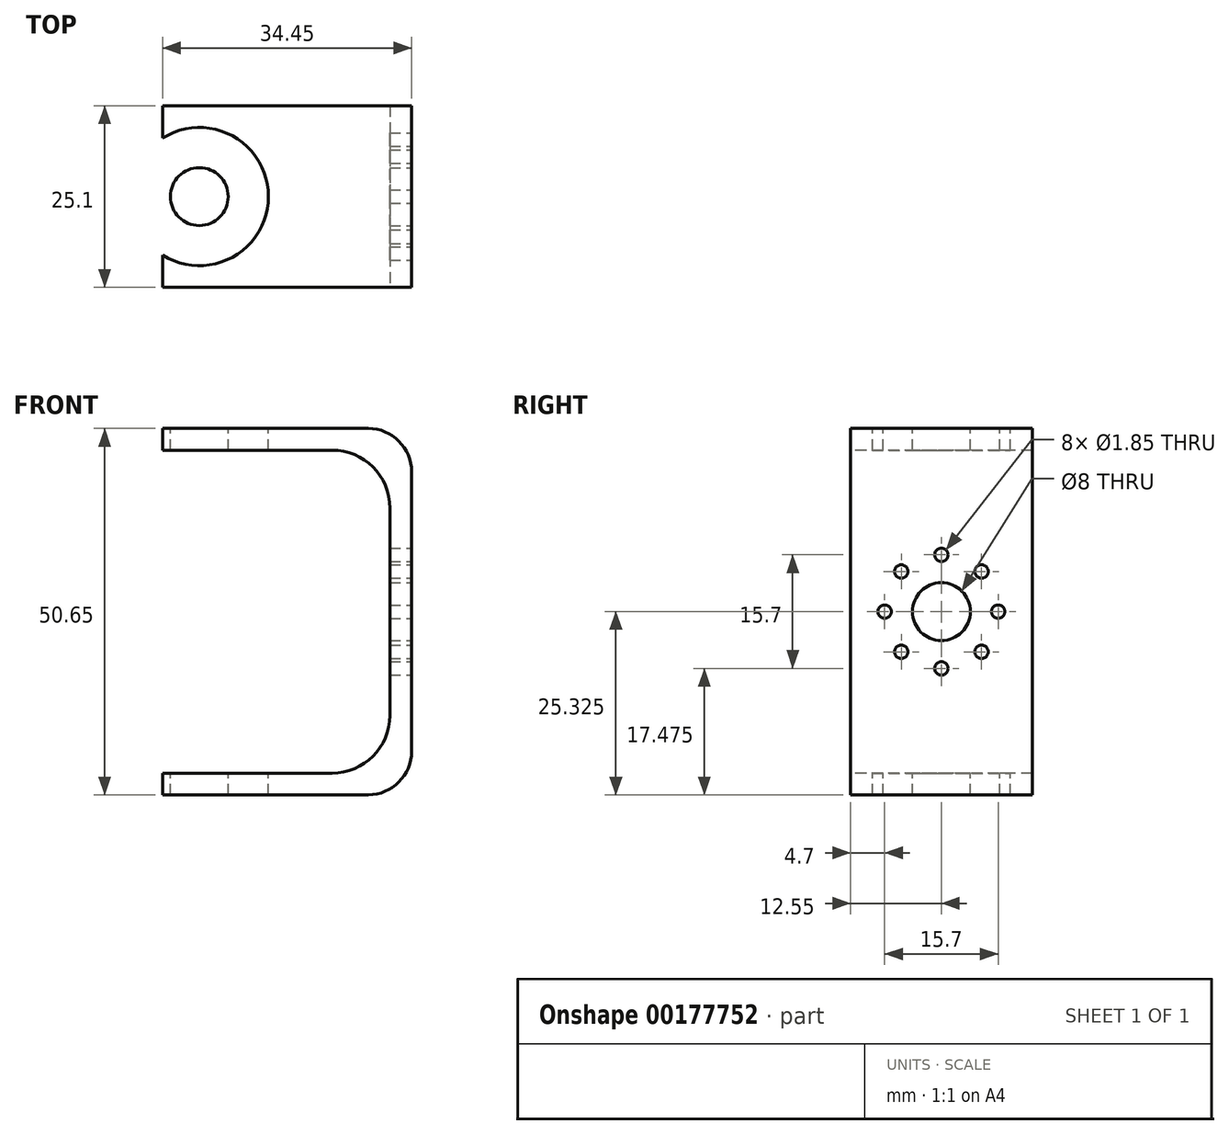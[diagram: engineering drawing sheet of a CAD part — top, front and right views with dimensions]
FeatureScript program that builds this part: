
annotation { "Feature Type Name" : "Feature", "Feature Type Description" : "" }
export const myFeature = defineFeature(function(context is Context, id is Id, definition is map)
    precondition{}
    {
        {
            var Q0;
            Q0=qCreatedBy(makeId("Top.planeOp"),FACE);
            var sketch = newSketch(context, id + "F0", { "sketchPlane" : qUnion([Q0])});
            skLineSegment(sketch, "E0.bottom", {"start": v(-15.32, 25.1) * mm, "end": v(19.13, 25.1) * mm});
            skLineSegment(sketch, "E0.top", {"start": v(-15.32, 0) * mm, "end": v(19.13, 0) * mm});
            skLineSegment(sketch, "E0.left", {"start": v(-15.32, 25.1) * mm, "end": v(-15.32, 0) * mm});
            skLineSegment(sketch, "E0.right", {"start": v(19.13, 25.1) * mm, "end": v(19.13, 0) * mm});
            skSolve(sketch);
        }
        {
            var Q0;
            Q0=qSketchRegion(id+"F0",true);
            extrude(context, id + "F1", {"entities" : qUnion([Q0]), "depth" : 50.65 * mm});
        }
        {
            var Q0;
            Q0=makeQuery(id+"F1.opExtrude","SWEPT_FACE",FACE,{"disambiguationData":[OSD([sQuery(id+"F0.wireOp",EDGE,"E0.left")])]});
            shell(context, id + "F2", {"entities" : qUnion([Q0]), "thickness" : 3 * mm});
        }
        {
            var Q0;
            Q0=makeQuery(id+"F1.opExtrude","SWEPT_FACE",FACE,{"disambiguationData":[OSD([sQuery(id+"F0.wireOp",EDGE,"E0.right")])]});
            var sketch = newSketch(context, id + "F3", { "sketchPlane" : qUnion([Q0])});
            skLineSegment(sketch, "E1", {"start": v(12.55, 0) * mm, "end": v(12.55, 50.65) * mm, "construction": true});
            skCircle(sketch, "E2", {"center": v(12.55, 25.32) * mm, "radius": 4 * mm});
            skCircle(sketch, "E3", {"center": v(12.55, 17.48) * mm, "radius": 0.93 * mm});
            skCircle(sketch, "E4.1.0", {"center": v(18.1, 19.77) * mm, "radius": 0.92 * mm});
            skCircle(sketch, "E4.2.0", {"center": v(20.4, 25.32) * mm, "radius": 0.93 * mm});
            skCircle(sketch, "E4.3.0", {"center": v(18.1, 30.88) * mm, "radius": 0.93 * mm});
            skCircle(sketch, "E5.1.4.0", {"center": v(12.55, 33.18) * mm, "radius": 0.93 * mm});
            skCircle(sketch, "E5.1.5.0", {"center": v(7, 30.88) * mm, "radius": 0.93 * mm});
            skCircle(sketch, "E5.1.6.0", {"center": v(4.7, 25.32) * mm, "radius": 0.92 * mm});
            skCircle(sketch, "E5.1.7.0", {"center": v(7, 19.77) * mm, "radius": 0.93 * mm});
            skSolve(sketch);
        }
        {
            var Q0;
            Q0=qSketchRegion(id+"F3",true);
            extrude(context, id + "F4", {"entities" : qUnion([Q0]), "operationType" : NewBodyOperationType.REMOVE, "oppositeDirection" : true, "depth" : 25 * mm});
        }
        {
            var Q0;
            Q0=makeQuery(id+"F1.opExtrude","SWEPT_FACE",FACE,{"disambiguationData":[OSD([sQuery(id+"F0.wireOp",EDGE,"E0.bottom")])]});
            var sketch = newSketch(context, id + "F5", { "sketchPlane" : qUnion([Q0])});
            skLineSegment(sketch, "E6", {"start": v(15.32, 3) * mm, "end": v(-16.13, 3) * mm});
            skLineSegment(sketch, "E7", {"start": v(-16.13, 3) * mm, "end": v(-16.13, 47.65) * mm});
            skLineSegment(sketch, "E8", {"start": v(-16.13, 47.65) * mm, "end": v(15.32, 47.65) * mm});
            skSolve(sketch);
        }
        {
            var Q0;
            {var subQ0=sQuery(id+"F5.wireOp",EDGE,"E6");Q0=makeQuery(id+"F5.imprint","IMPRINT",FACE,{"disambiguationData":[TD([[makeQuery(id+"F5.imprint","IMPRINT",EDGE,{"derivedFrom":subQ0}),-1.0]])]});}
            extrude(context, id + "F6", {"entities" : qUnion([Q0]), "operationType" : NewBodyOperationType.REMOVE, "endBound" : BoundingType.THROUGH_ALL, "oppositeDirection" : true, "depth" : 25 * mm});
        }
        {
            var Q0;
            {var subQ0=sQuery(id+"F0.wireOp",EDGE,"E0.right");Q0=makeQuery(id+"F6.boolean.opBoolean","MERGE",EDGE,{"derivedFrom":[makeQuery(id+"F2.opShell","OFFSET_EDGE",EDGE,{"disambiguationData":[OSD([subQ0]),TDD([makeQuery(id+"F1.opExtrude","CAP_EDGE",EDGE,{"disambiguationData":[OSD([subQ0])],"isStart":false})])]}),makeQuery(id+"F6.opExtrude","SWEPT_EDGE",EDGE,{"disambiguationData":[OSD([sQuery(id+"F5.wireOp",EDGE,"E7"),sQuery(id+"F5.wireOp",EDGE,"E8")])]})]});}
            var Q1;
            {var subQ0=sQuery(id+"F0.wireOp",EDGE,"E0.right");Q1=makeQuery(id+"F6.boolean.opBoolean","MERGE",EDGE,{"derivedFrom":[makeQuery(id+"F2.opShell","OFFSET_EDGE",EDGE,{"disambiguationData":[OSD([subQ0]),TDD([makeQuery(id+"F1.opExtrude","CAP_EDGE",EDGE,{"disambiguationData":[OSD([subQ0])],"isStart":true})])]}),makeQuery(id+"F6.opExtrude","SWEPT_EDGE",EDGE,{"disambiguationData":[OSD([sQuery(id+"F5.wireOp",EDGE,"E6"),sQuery(id+"F5.wireOp",EDGE,"E7")])]})]});}
            fillet(context, id + "F7", {"entities" : qUnion([Q0, Q1]), "radius" : 8 * mm, "tangentPropagation" : true, "allowEdgeOverflow" : false});
        }
        {
            var Q0;
            Q0=makeQuery(id+"F1.opExtrude","CAP_EDGE",EDGE,{"disambiguationData":[OSD([sQuery(id+"F0.wireOp",EDGE,"E0.right")])],"isStart":false});
            var Q1;
            Q1=makeQuery(id+"F1.opExtrude","CAP_EDGE",EDGE,{"disambiguationData":[OSD([sQuery(id+"F0.wireOp",EDGE,"E0.right")])],"isStart":true});
            fillet(context, id + "F8", {"entities" : qUnion([Q0, Q1]), "radius" : 6 * mm, "tangentPropagation" : true, "allowEdgeOverflow" : false});
        }
        {
            var Q0;
            Q0=makeQuery(id+"F1.opExtrude","CAP_FACE",FACE,{"disambiguationData":[OSD([sQuery(id+"F0.wireOp",EDGE,"E0.bottom"),sQuery(id+"F0.wireOp",EDGE,"E0.top"),sQuery(id+"F0.wireOp",EDGE,"E0.left"),sQuery(id+"F0.wireOp",EDGE,"E0.right")])],"isStart":false});
            var sketch = newSketch(context, id + "F9", { "sketchPlane" : qUnion([Q0])});
            skLineSegment(sketch, "E9", {"start": v(-15.32, 0) * mm, "end": v(-15.32, 25.1) * mm, "construction": true});
            skLineSegment(sketch, "E10", {"start": v(19.13, 25.1) * mm, "end": v(19.13, 0) * mm, "construction": true});
            skLineSegment(sketch, "E11", {"start": v(16.13, 0) * mm, "end": v(16.13, 25.1) * mm, "construction": true});
            skLineSegment(sketch, "E12.0", {"start": v(-15.32, 3) * mm, "end": v(19.13, 3) * mm});
            skLineSegment(sketch, "E12.1", {"start": v(-15.32, 3) * mm, "end": v(-15.32, 22.1) * mm});
            skLineSegment(sketch, "E12.2", {"start": v(-15.32, 22.1) * mm, "end": v(19.13, 22.1) * mm});
            skLineSegment(sketch, "E13", {"start": v(-15.32, 12.55) * mm, "end": v(19.13, 12.55) * mm});
            skPoint(sketch, "E13.endSnap0", {"position": v(-15.32, 12.55) * mm});
            skCircle(sketch, "E14", {"center": v(-10.22, 12.55) * mm, "radius": 4 * mm});
            skCircle(sketch, "E15", {"center": v(-10.22, 12.55) * mm, "radius": 9.55 * mm});
            skCircle(sketch, "E16", {"center": v(-3.12, 12.55) * mm, "radius": 0.93 * mm});
            skPoint(sketch, "E17", {"position": v(-0.67, 12.55) * mm});
            skCircle(sketch, "E18.1.0", {"center": v(-10.22, 19.65) * mm, "radius": 0.93 * mm});
            skCircle(sketch, "E18.2.0", {"center": v(-17.32, 12.55) * mm, "radius": 0.93 * mm});
            skCircle(sketch, "E18.3.0", {"center": v(-10.22, 5.45) * mm, "radius": 0.93 * mm});
            skLineSegment(sketch, "E19", {"start": v(-10.22, 8.55) * mm, "end": v(-18.9, 8.55) * mm});
            skLineSegment(sketch, "E20", {"start": v(-10.22, 16.55) * mm, "end": v(-15.32, 16.55) * mm});
            skLineSegment(sketch, "E21", {"start": v(19.13, 22.1) * mm, "end": v(-15.32, 22.1) * mm, "construction": true});
            skLineSegment(sketch, "E22", {"start": v(-15.32, 3) * mm, "end": v(19.13, 3) * mm, "construction": true});
            skSolve(sketch);
        }
        {
            var Q0;
            Q0=makeQuery(id+"F9.imprint","IMPRINT",FACE,{"disambiguationData":[TD([[makeQuery(id+"F9.imprint","IMPRINT",EDGE,{"derivedFrom":sQuery(id+"F9.wireOp",EDGE,"E18.1.0")}),1.0]])]});
            var Q1;
            Q1=makeQuery(id+"F9.imprint","IMPRINT",FACE,{"disambiguationData":[TD([[makeQuery(id+"F9.imprint","IMPRINT",EDGE,{"derivedFrom":sQuery(id+"F9.wireOp",EDGE,"E18.3.0")}),1.0]])]});
            var Q2;
            {var subQ0=sQuery(id+"F9.wireOp",EDGE,"E16");var subQ1=sQuery(id+"F9.wireOp",EDGE,"E13");var subQ2=makeQuery(id+"F9.imprint","INTERSECT",VERTEX,{"disambiguationData":[OD(0.0)],"derivedFrom":[subQ1,subQ0]});Q2=makeQuery(id+"F9.imprint","IMPRINT",FACE,{"disambiguationData":[TD([[makeQuery(id+"F9.imprint","IMPRINT",EDGE,{"disambiguationData":[TD([[subQ2,-1.0]])],"derivedFrom":subQ1}),1.0]])]});}
            var Q3;
            {var subQ0=sQuery(id+"F9.wireOp",EDGE,"E16");var subQ1=sQuery(id+"F9.wireOp",EDGE,"E13");var subQ2=makeQuery(id+"F9.imprint","INTERSECT",VERTEX,{"disambiguationData":[OD(0.0)],"derivedFrom":[subQ1,subQ0]});Q3=makeQuery(id+"F9.imprint","IMPRINT",FACE,{"disambiguationData":[TD([[makeQuery(id+"F9.imprint","IMPRINT",EDGE,{"disambiguationData":[TD([[subQ2,-1.0]])],"derivedFrom":subQ1}),-1.0]])]});}
            var Q4;
            {var subQ0=sQuery(id+"F9.wireOp",EDGE,"E14");var subQ1=sQuery(id+"F9.wireOp",EDGE,"E13");var subQ2=makeQuery(id+"F9.imprint","INTERSECT",VERTEX,{"disambiguationData":[OD(0.0)],"derivedFrom":[subQ1,subQ0]});Q4=makeQuery(id+"F9.imprint","IMPRINT",FACE,{"disambiguationData":[TD([[makeQuery(id+"F9.imprint","IMPRINT",EDGE,{"disambiguationData":[TD([[subQ2,-1.0]])],"derivedFrom":subQ1}),1.0]])]});}
            var Q5;
            {var subQ0=sQuery(id+"F9.wireOp",EDGE,"E14");var subQ1=sQuery(id+"F9.wireOp",EDGE,"E13");var subQ2=makeQuery(id+"F9.imprint","INTERSECT",VERTEX,{"disambiguationData":[OD(0.0)],"derivedFrom":[subQ1,subQ0]});Q5=makeQuery(id+"F9.imprint","IMPRINT",FACE,{"disambiguationData":[TD([[makeQuery(id+"F9.imprint","IMPRINT",EDGE,{"disambiguationData":[TD([[subQ2,-1.0]])],"derivedFrom":subQ1}),-1.0]])]});}
            var Q6;
            {var subQ3=sQuery(id+"F9.wireOp",EDGE,"E20");Q6=makeQuery(id+"F9.imprint","IMPRINT",FACE,{"disambiguationData":[TD([[makeQuery(id+"F9.imprint","IMPRINT",EDGE,{"derivedFrom":subQ3}),1.0]])]});}
            var Q7;
            {var subQ0=sQuery(id+"F9.wireOp",EDGE,"E13");var subQ1=sQuery(id+"F9.wireOp",EDGE,"E12.1");var subQ2=makeQuery(id+"F9.imprint","INTERSECT",VERTEX,{"derivedFrom":[subQ1,subQ0]});Q7=makeQuery(id+"F9.imprint","IMPRINT",FACE,{"disambiguationData":[TD([[makeQuery(id+"F9.imprint","IMPRINT",EDGE,{"disambiguationData":[TD([[subQ2,-1.0]])],"derivedFrom":subQ1}),1.0]])]});}
            extrude(context, id + "F10", {"entities" : qUnion([Q0, Q1, Q2, Q3, Q4, Q5, Q6, Q7]), "operationType" : NewBodyOperationType.REMOVE, "endBound" : BoundingType.THROUGH_ALL, "oppositeDirection" : true, "depth" : 25 * mm});
        }
    });
